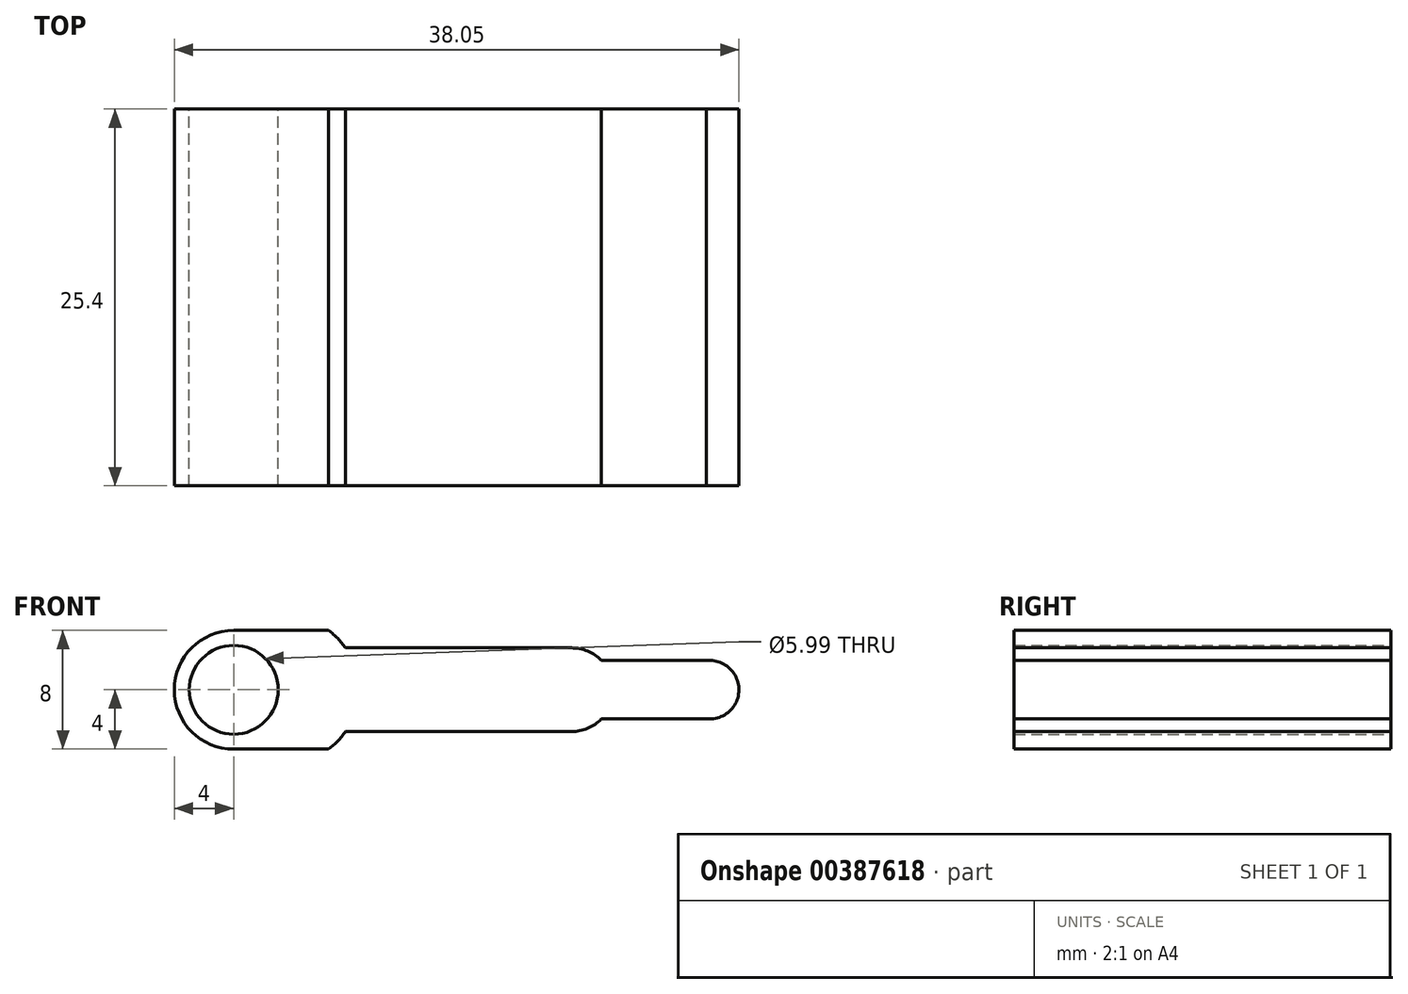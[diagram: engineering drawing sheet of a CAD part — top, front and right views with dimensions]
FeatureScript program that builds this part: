
annotation { "Feature Type Name" : "Feature", "Feature Type Description" : "" }
export const myFeature = defineFeature(function(context is Context, id is Id, definition is map)
    precondition{}
    {
        {
            var Q0;
            Q0=qCreatedBy(makeId("Front.planeOp"),FACE);
            var sketch = newSketch(context, id + "F0", { "sketchPlane" : qUnion([Q0])});
            skCircle(sketch, "E0", {"center": v(0, 0) * mm, "radius": 4 * mm});
            skCircle(sketch, "E1", {"center": v(0, 0) * mm, "radius": 3 * mm});
            skLineSegment(sketch, "E2", {"start": v(0, 4) * mm, "end": v(6.4, 4) * mm});
            skLineSegment(sketch, "E3", {"start": v(0, -4) * mm, "end": v(6.4, -4) * mm});
            skArc(sketch, "E4", {"start": v(6.4, -4) * mm, "mid": v(8.41, 0) * mm, "end": v(6.4, 4) * mm});
            skLineSegment(sketch, "E5", {"start": v(7.53, 2.83) * mm, "end": v(22.76, 2.83) * mm});
            skLineSegment(sketch, "E6", {"start": v(7.54, -2.82) * mm, "end": v(22.76, -2.82) * mm});
            skArc(sketch, "E7", {"start": v(22.76, -2.82) * mm, "mid": v(25.58, 0) * mm, "end": v(22.76, 2.83) * mm});
            skLineSegment(sketch, "E8", {"start": v(20.74, 1.97) * mm, "end": v(31.87, 1.97) * mm});
            skLineSegment(sketch, "E9", {"start": v(24.78, -1.97) * mm, "end": v(32.07, -1.97) * mm});
            skArc(sketch, "E10", {"start": v(32.07, -1.97) * mm, "mid": v(34.05, 0.11) * mm, "end": v(31.87, 1.97) * mm});
            skLineSegment(sketch, "E11", {"start": v(31.87, 1.97) * mm, "end": v(32.07, -1.97) * mm});
            skSolve(sketch);
        }
        {
            var Q0;
            Q0 = qSketchRegion(id + "F0", true);
            extrude(context, id + "F1", {"entities" : qUnion([Q0]), "depth" : 25.4 * mm});
        }
    });
